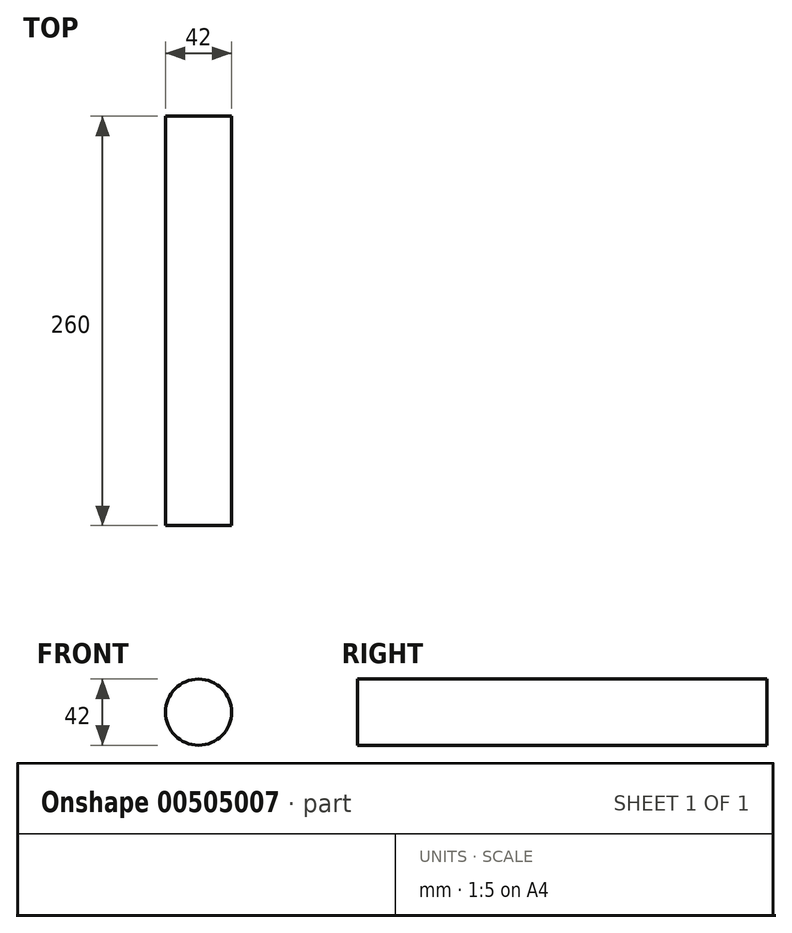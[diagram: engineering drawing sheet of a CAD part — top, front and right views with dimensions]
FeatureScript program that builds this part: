
annotation { "Feature Type Name" : "Feature", "Feature Type Description" : "" }
export const myFeature = defineFeature(function(context is Context, id is Id, definition is map)
    precondition{}
    {
        {
            var Q0;
            Q0=qCreatedBy(makeId("Front.planeOp"),FACE);
            var sketch = newSketch(context, id + "F0", { "sketchPlane" : qUnion([Q0])});
            skCircle(sketch, "E0", {"center": v(0, 0) * mm, "radius": 21 * mm});
            skSolve(sketch);
        }
        {
            var Q0;
            Q0=makeQuery(id+"F0.imprint","IMPRINT",FACE,{"disambiguationData":[TD([[makeQuery(id+"F0.imprint","IMPRINT",EDGE,{"derivedFrom":sQuery(id+"F0.wireOp",EDGE,"E0")}),1.0]])]});
            extrude(context, id + "F1", {"entities" : qUnion([Q0]), "depth" : 260 * mm});
        }
    });
